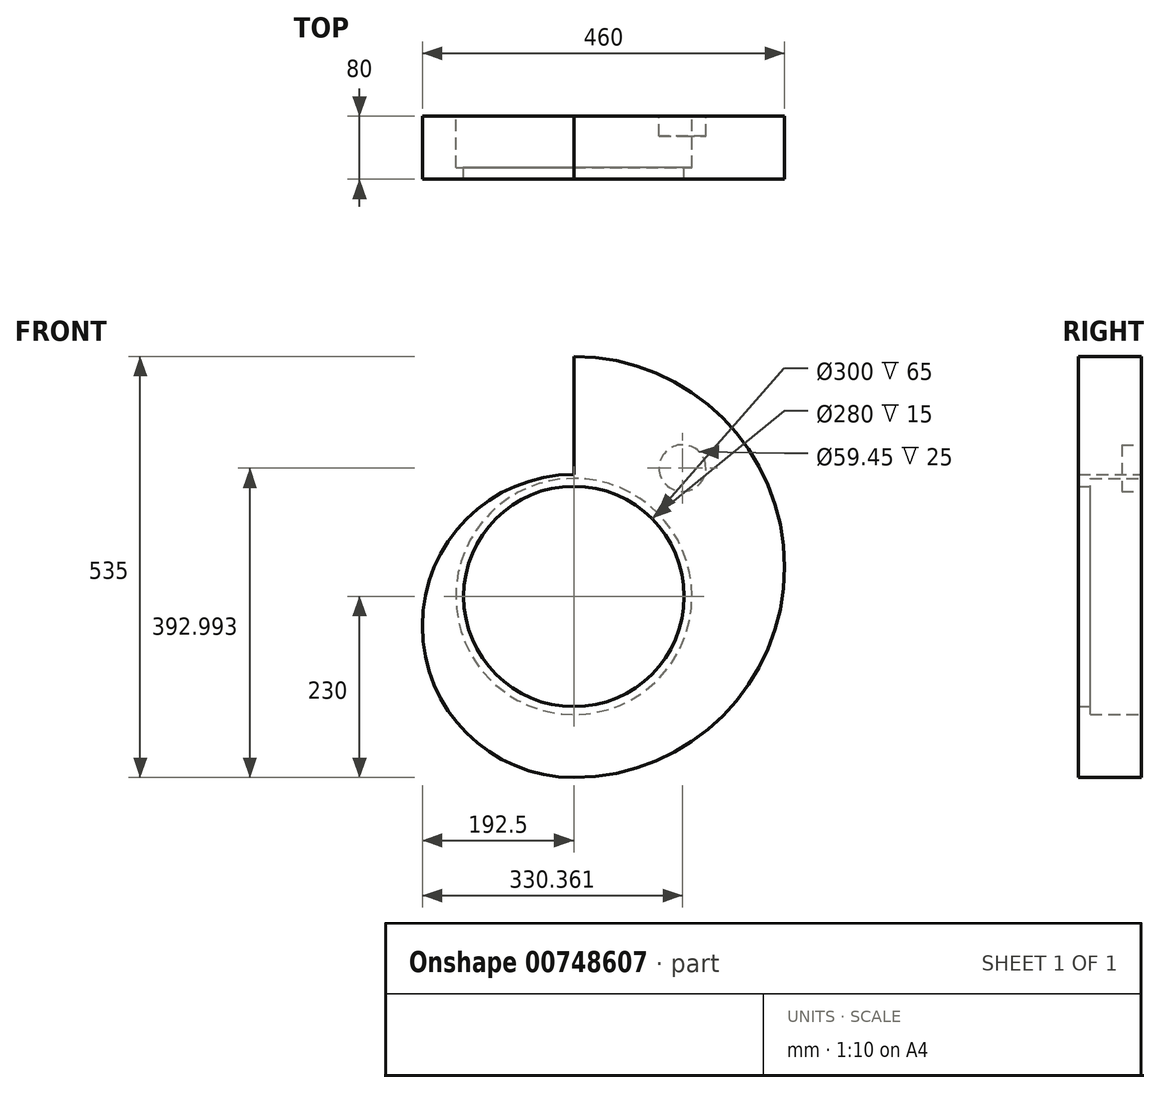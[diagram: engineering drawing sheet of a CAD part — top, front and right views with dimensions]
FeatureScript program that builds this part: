
annotation { "Feature Type Name" : "Feature", "Feature Type Description" : "" }
export const myFeature = defineFeature(function(context is Context, id is Id, definition is map)
    precondition{}
    {
        {
            var Q0;
            Q0=qCreatedBy(makeId("Front.planeOp"),FACE);
            var sketch = newSketch(context, id + "F0", { "sketchPlane" : qUnion([Q0])});
            skCircle(sketch, "E0", {"center": v(0, 0) * mm, "radius": 155 * mm, "construction": true});
            skArc(sketch, "E1", {"start": v(0, 155) * mm, "mid": v(-192.5, -37.5) * mm, "end": v(0, -230) * mm});
            skArc(sketch, "E2", {"start": v(0, -230) * mm, "mid": v(267.5, 37.5) * mm, "end": v(0, 305) * mm});
            skLineSegment(sketch, "E3", {"start": v(0, 155) * mm, "end": v(0, 305) * mm});
            skCircle(sketch, "E4", {"center": v(0, 0) * mm, "radius": 150 * mm});
            skSolve(sketch);
        }
        {
            var Q0;
            Q0=makeQuery(id+"F0.imprint","IMPRINT",FACE,{"disambiguationData":[TD([[makeQuery(id+"F0.imprint","IMPRINT",EDGE,{"derivedFrom":sQuery(id+"F0.wireOp",EDGE,"E1")}),1.0]])]});
            var Q1;
            Q1=makeQuery(id+"F0.imprint","IMPRINT",FACE,{"disambiguationData":[TD([[makeQuery(id+"F0.imprint","IMPRINT",EDGE,{"derivedFrom":sQuery(id+"F0.wireOp",EDGE,"E4")}),1.0]])]});
            extrude(context, id + "F1", {"entities" : qUnion([Q0, Q1]), "depth" : 80 * mm, "offsetDistance" : 25 * mm});
        }
        {
            var Q0;
            Q0=qCreatedBy(makeId("Front.planeOp"),FACE);
            var sketch = newSketch(context, id + "F2", { "sketchPlane" : qUnion([Q0])});
            skCircle(sketch, "E5", {"center": v(0, 0) * mm, "radius": 150 * mm});
            skSolve(sketch);
        }
        {
            var Q0;
            Q0 = qSketchRegion(id + "F2", true);
            extrude(context, id + "F3", {"entities" : qUnion([Q0]), "operationType" : NewBodyOperationType.REMOVE, "depth" : 65 * mm, "offsetDistance" : 25 * mm});
        }
        {
            var Q0;
            Q0=qCreatedBy(makeId("Front.planeOp"),FACE);
            var sketch = newSketch(context, id + "F4", { "sketchPlane" : qUnion([Q0])});
            skCircle(sketch, "E6", {"center": v(0, 0) * mm, "radius": 140 * mm});
            skSolve(sketch);
        }
        {
            var Q0;
            Q0 = qSketchRegion(id + "F4", true);
            extrude(context, id + "F5", {"entities" : qUnion([Q0]), "operationType" : NewBodyOperationType.REMOVE, "endBound" : BoundingType.THROUGH_ALL, "depth" : 25 * mm, "offsetDistance" : 25 * mm});
        }
        {
            var Q0;
            Q0=makeQuery(id+"F1.opExtrude","CAP_FACE",FACE,{"disambiguationData":[OSD([sQuery(id+"F0.wireOp",EDGE,"E1"),sQuery(id+"F0.wireOp",EDGE,"E2"),sQuery(id+"F0.wireOp",EDGE,"E3")])],"isStart":true});
            var sketch = newSketch(context, id + "F6", { "sketchPlane" : qUnion([Q0])});
            skCircle(sketch, "E7", {"center": v(-137.86, 163) * mm, "radius": 29.73 * mm});
            skSolve(sketch);
        }
        {
            var Q0;
            Q0 = qSketchRegion(id + "F6", true);
            extrude(context, id + "F7", {"entities" : qUnion([Q0]), "operationType" : NewBodyOperationType.REMOVE, "oppositeDirection" : true, "depth" : 25 * mm, "offsetDistance" : 25 * mm});
        }
    });
